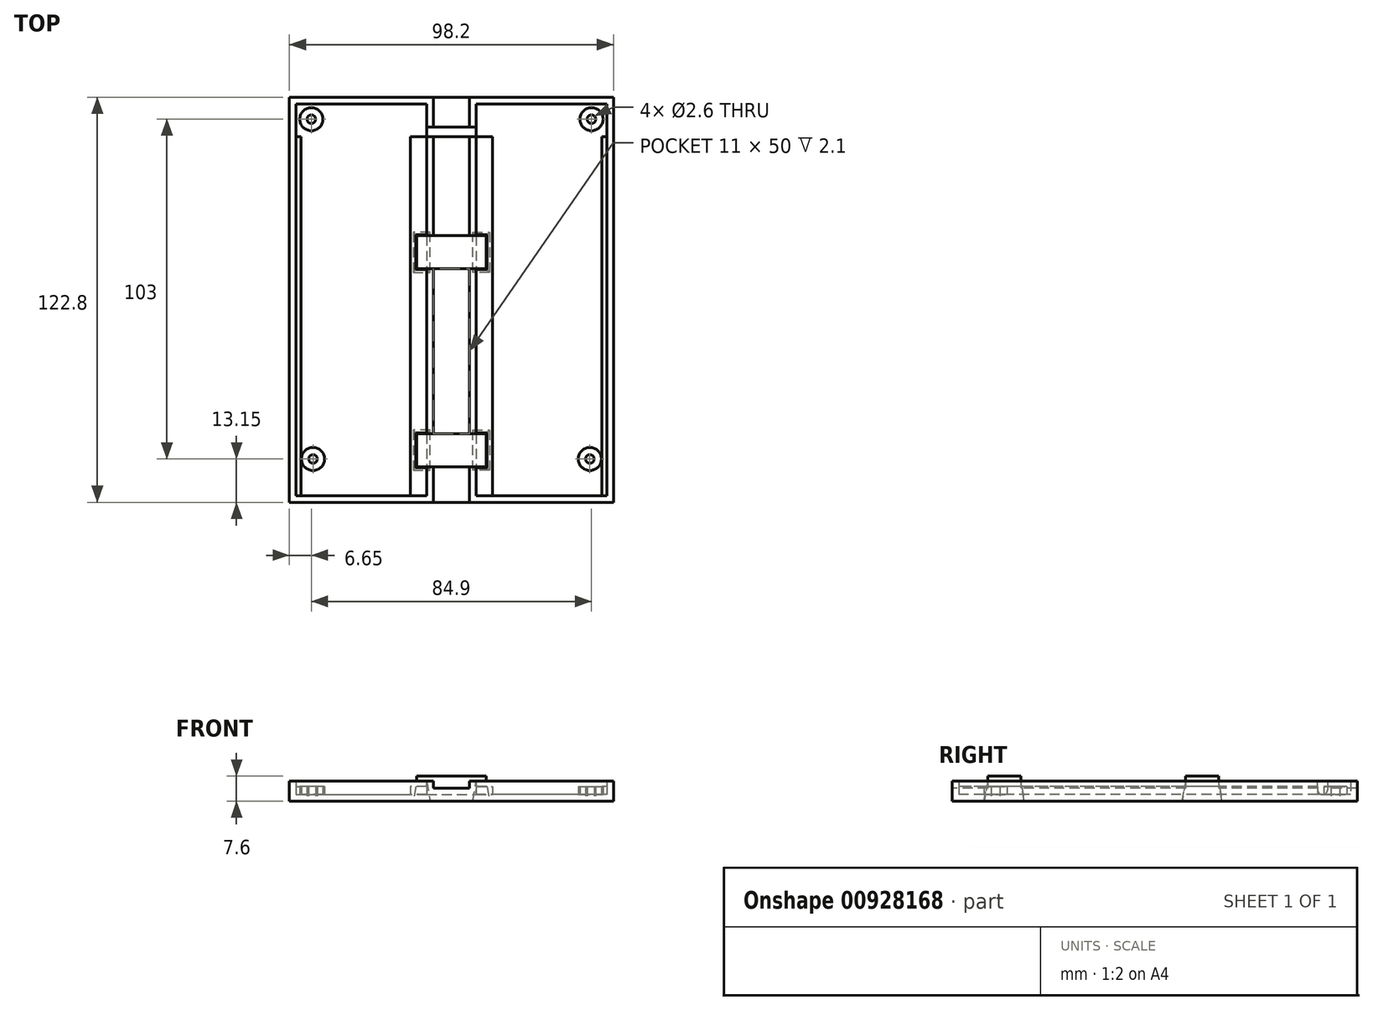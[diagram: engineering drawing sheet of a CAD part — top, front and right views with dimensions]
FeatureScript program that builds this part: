
annotation { "Feature Type Name" : "Feature", "Feature Type Description" : "" }
export const myFeature = defineFeature(function(context is Context, id is Id, definition is map)
    precondition{}
    {
        {
            var Q0;
            Q0=qCreatedBy(makeId("Top.planeOp"),FACE);
            var sketch = newSketch(context, id + "F0", { "sketchPlane" : qUnion([Q0])});
            skLineSegment(sketch, "E0.bottom", {"start": v(-49.1, 61.4) * mm, "end": v(-5.5, 61.4) * mm});
            skLineSegment(sketch, "E0.top", {"start": v(-49.1, -61.4) * mm, "end": v(-5.5, -61.4) * mm});
            skLineSegment(sketch, "E0.left", {"start": v(-49.1, 61.4) * mm, "end": v(-49.1, -61.4) * mm});
            skLineSegment(sketch, "E0.right", {"start": v(-5.5, 61.4) * mm, "end": v(-5.5, -61.4) * mm});
            skLineSegment(sketch, "E1", {"start": v(-5.5, 61.4) * mm, "end": v(0, 61.4) * mm});
            skLineSegment(sketch, "E2", {"start": v(0, 61.4) * mm, "end": v(0, -61.4) * mm});
            skLineSegment(sketch, "E3", {"start": v(0, -61.4) * mm, "end": v(-5.5, -61.4) * mm});
            skSolve(sketch);
        }
        {
            var Q0;
            Q0=makeQuery(id+"F0.imprint","IMPRINT",FACE,{"disambiguationData":[TD([[makeQuery(id+"F0.imprint","IMPRINT",EDGE,{"derivedFrom":sQuery(id+"F0.wireOp",EDGE,"E0.bottom")}),-1.0]])]});
            extrude(context, id + "F1", {"entities" : qUnion([Q0]), "depth" : 6.1 * mm, "offsetDistance" : 25 * mm});
        }
        {
            var Q0;
            Q0=makeQuery(id+"F1.opExtrude","CAP_FACE",FACE,{"disambiguationData":[OSD([sQuery(id+"F0.wireOp",EDGE,"E0.bottom"),sQuery(id+"F0.wireOp",EDGE,"E0.top"),sQuery(id+"F0.wireOp",EDGE,"E0.left"),sQuery(id+"F0.wireOp",EDGE,"E0.right")])],"isStart":false});
            shell(context, id + "F2", {"entities" : qUnion([Q0]), "thickness" : 2 * mm});
        }
        {
            var Q0;
            Q0=makeQuery(id+"F2.opShell","OFFSET_FACE",FACE,{"disambiguationData":[OSD([sQuery(id+"F0.wireOp",EDGE,"E0.bottom"),sQuery(id+"F0.wireOp",EDGE,"E0.top"),sQuery(id+"F0.wireOp",EDGE,"E0.left"),sQuery(id+"F0.wireOp",EDGE,"E0.right")])]});
            var sketch = newSketch(context, id + "F3", { "sketchPlane" : qUnion([Q0])});
            skCircle(sketch, "E4", {"center": v(-42.45, 54.75) * mm, "radius": 3.5 * mm});
            skCircle(sketch, "E5", {"center": v(-42.45, 54.75) * mm, "radius": 1.3 * mm});
            skLineSegment(sketch, "E6", {"start": v(-42.45, 54.75) * mm, "end": v(-47.1, 54.75) * mm, "construction": true});
            skLineSegment(sketch, "E7", {"start": v(-42.45, 54.75) * mm, "end": v(-42.45, 59.4) * mm, "construction": true});
            skCircle(sketch, "E8", {"center": v(-41.95, -48.25) * mm, "radius": 3.5 * mm});
            skCircle(sketch, "E9", {"center": v(-41.95, -48.25) * mm, "radius": 1.3 * mm});
            skLineSegment(sketch, "E10", {"start": v(-42.45, 54.75) * mm, "end": v(-42.45, -48.25) * mm, "construction": true});
            skLineSegment(sketch, "E11", {"start": v(-42.45, -48.25) * mm, "end": v(-41.95, -48.25) * mm, "construction": true});
            skSolve(sketch);
        }
        {
            var Q0;
            Q0 = qSketchRegion(id + "F3", true);
            var Q1;
            Q1=makeQuery(id+"F1.opExtrude","CAP_FACE",FACE,{"disambiguationData":[OSD([sQuery(id+"F0.wireOp",EDGE,"E0.bottom"),sQuery(id+"F0.wireOp",EDGE,"E0.top"),sQuery(id+"F0.wireOp",EDGE,"E0.left"),sQuery(id+"F0.wireOp",EDGE,"E0.right")])],"isStart":false});
            extrude(context, id + "F4", {"entities" : qUnion([Q0]), "operationType" : NewBodyOperationType.ADD, "endBound" : BoundingType.UP_TO_SURFACE, "depth" : 25 * mm, "endBoundEntityFace" : qUnion([Q1]), "hasOffset" : true, "offsetDistance" : 1.6 * mm});
        }
        {
            var Q0;
            Q0=makeQuery(id+"F4.boolean.opBoolean","SPLIT",FACE,{"disambiguationData":[TD([makeQuery(id+"F4.opExtrude","SWEPT_FACE",FACE,{"disambiguationData":[OSD([sQuery(id+"F3.wireOp",EDGE,"E5")])]})])],"derivedFrom":makeQuery(id+"F2.opShell","OFFSET_FACE",FACE,{"disambiguationData":[OSD([sQuery(id+"F0.wireOp",EDGE,"E0.bottom"),sQuery(id+"F0.wireOp",EDGE,"E0.top"),sQuery(id+"F0.wireOp",EDGE,"E0.left"),sQuery(id+"F0.wireOp",EDGE,"E0.right")])]})});
            var Q1;
            Q1=makeQuery(id+"F4.boolean.opBoolean","SPLIT",FACE,{"disambiguationData":[TD([makeQuery(id+"F4.opExtrude","SWEPT_FACE",FACE,{"disambiguationData":[OSD([sQuery(id+"F3.wireOp",EDGE,"E9")])]})])],"derivedFrom":makeQuery(id+"F2.opShell","OFFSET_FACE",FACE,{"disambiguationData":[OSD([sQuery(id+"F0.wireOp",EDGE,"E0.bottom"),sQuery(id+"F0.wireOp",EDGE,"E0.top"),sQuery(id+"F0.wireOp",EDGE,"E0.left"),sQuery(id+"F0.wireOp",EDGE,"E0.right")])]})});
            extrude(context, id + "F5", {"entities" : qUnion([Q0, Q1]), "operationType" : NewBodyOperationType.REMOVE, "endBound" : BoundingType.THROUGH_ALL, "oppositeDirection" : true, "depth" : 25 * mm, "offsetDistance" : 25 * mm});
        }
        {
            var Q0;
            {var subQ0=sQuery(id+"F0.wireOp",EDGE,"E0.right");var subQ1=sQuery(id+"F0.wireOp",EDGE,"E0.left");var subQ2=sQuery(id+"F0.wireOp",EDGE,"E0.top");var subQ3=sQuery(id+"F0.wireOp",EDGE,"E0.bottom");Q0=makeQuery(id+"F4.boolean.opBoolean","SPLIT",FACE,{"disambiguationData":[TD([makeQuery(id+"F2.opShell","OFFSET_FACE",FACE,{"disambiguationData":[OSD([subQ3])]})])],"derivedFrom":makeQuery(id+"F2.opShell","OFFSET_FACE",FACE,{"disambiguationData":[OSD([subQ3,subQ2,subQ1,subQ0])]})});}
            var sketch = newSketch(context, id + "F6", { "sketchPlane" : qUnion([Q0])});
            skLineSegment(sketch, "E12.bottom", {"start": v(-47.1, 49.4) * mm, "end": v(-45.6, 49.4) * mm});
            skLineSegment(sketch, "E12.top", {"start": v(-47.1, -59.4) * mm, "end": v(-45.6, -59.4) * mm});
            skLineSegment(sketch, "E12.left", {"start": v(-47.1, 49.4) * mm, "end": v(-47.1, -59.4) * mm});
            skLineSegment(sketch, "E12.right", {"start": v(-45.6, 49.4) * mm, "end": v(-45.6, -59.4) * mm});
            skLineSegment(sketch, "E13.bottom", {"start": v(-7.5, 49.4) * mm, "end": v(-12.5, 49.4) * mm});
            skLineSegment(sketch, "E13.top", {"start": v(-7.5, -59.4) * mm, "end": v(-12.5, -59.4) * mm});
            skLineSegment(sketch, "E13.left", {"start": v(-7.5, 49.4) * mm, "end": v(-7.5, -59.4) * mm});
            skLineSegment(sketch, "E13.right", {"start": v(-12.5, 49.4) * mm, "end": v(-12.5, -59.4) * mm});
            skLineSegment(sketch, "E14", {"start": v(-45.6, 49.4) * mm, "end": v(-12.5, 49.4) * mm, "construction": true});
            skSolve(sketch);
        }
        {
            var Q0;
            Q0 = qSketchRegion(id + "F6", true);
            var Q1;
            Q1=makeQuery(id+"F4.opExtrude","CAP_FACE",FACE,{"disambiguationData":[OSD([sQuery(id+"F3.wireOp",EDGE,"E4"),sQuery(id+"F3.wireOp",EDGE,"E5")])],"isStart":false});
            extrude(context, id + "F7", {"entities" : qUnion([Q0]), "operationType" : NewBodyOperationType.ADD, "endBound" : BoundingType.UP_TO_SURFACE, "depth" : 25 * mm, "endBoundEntityFace" : qUnion([Q1]), "offsetDistance" : 25 * mm});
        }
        {
            var Q0;
            Q0=makeQuery(id+"F1.opExtrude","CAP_FACE",FACE,{"disambiguationData":[OSD([sQuery(id+"F0.wireOp",EDGE,"E0.bottom"),sQuery(id+"F0.wireOp",EDGE,"E0.top"),sQuery(id+"F0.wireOp",EDGE,"E0.left"),sQuery(id+"F0.wireOp",EDGE,"E0.right")])],"isStart":false});
            var sketch = newSketch(context, id + "F8", { "sketchPlane" : qUnion([Q0])});
            skLineSegment(sketch, "E15.bottom", {"start": v(-10.5, 19.4) * mm, "end": v(-5.5, 19.4) * mm});
            skLineSegment(sketch, "E15.top", {"start": v(-10.5, 9.4) * mm, "end": v(-5.5, 9.4) * mm});
            skLineSegment(sketch, "E15.left", {"start": v(-10.5, 19.4) * mm, "end": v(-10.5, 9.4) * mm});
            skLineSegment(sketch, "E15.right", {"start": v(-5.5, 19.4) * mm, "end": v(-5.5, 9.4) * mm});
            skLineSegment(sketch, "E16.bottom", {"start": v(-10.5, -40.6) * mm, "end": v(-5.5, -40.6) * mm});
            skLineSegment(sketch, "E16.top", {"start": v(-10.5, -50.6) * mm, "end": v(-5.5, -50.6) * mm});
            skLineSegment(sketch, "E16.left", {"start": v(-10.5, -40.6) * mm, "end": v(-10.5, -50.6) * mm});
            skLineSegment(sketch, "E16.right", {"start": v(-5.5, -40.6) * mm, "end": v(-5.5, -50.6) * mm});
            skLineSegment(sketch, "E17", {"start": v(-10.5, -40.6) * mm, "end": v(-10.5, 9.4) * mm, "construction": true});
            skSolve(sketch);
        }
        {
            var Q0;
            Q0 = qSketchRegion(id + "F8", true);
            extrude(context, id + "F9", {"entities" : qUnion([Q0]), "operationType" : NewBodyOperationType.ADD, "depth" : 1.5 * mm, "offsetDistance" : 25 * mm});
        }
        {
            var Q0;
            Q0=makeQuery(id+"F9.opExtrude","CAP_FACE",FACE,{"disambiguationData":[OSD([sQuery(id+"F8.wireOp",EDGE,"E15.bottom"),sQuery(id+"F8.wireOp",EDGE,"E15.top"),sQuery(id+"F8.wireOp",EDGE,"E15.left"),sQuery(id+"F8.wireOp",EDGE,"E15.right")])],"isStart":true});
            var sketch = newSketch(context, id + "F10", { "sketchPlane" : qUnion([Q0])});
            skLineSegment(sketch, "E18.bottom", {"start": v(-10.5, -19.4) * mm, "end": v(-7.5, -19.4) * mm});
            skLineSegment(sketch, "E18.top", {"start": v(-10.5, -9.4) * mm, "end": v(-7.5, -9.4) * mm});
            skLineSegment(sketch, "E18.left", {"start": v(-10.5, -19.4) * mm, "end": v(-10.5, -9.4) * mm});
            skLineSegment(sketch, "E18.right", {"start": v(-7.5, -19.4) * mm, "end": v(-7.5, -9.4) * mm});
            skPoint(sketch, "E19.0", {"position": v(-10.5, 40.6) * mm});
            skPoint(sketch, "E19.1", {"position": v(-7.5, 50.6) * mm});
            skLineSegment(sketch, "E20.bottom", {"start": v(-10.5, 40.6) * mm, "end": v(-7.5, 40.6) * mm});
            skLineSegment(sketch, "E20.top", {"start": v(-10.5, 50.6) * mm, "end": v(-7.5, 50.6) * mm});
            skLineSegment(sketch, "E20.left", {"start": v(-10.5, 40.6) * mm, "end": v(-10.5, 50.6) * mm});
            skLineSegment(sketch, "E20.right", {"start": v(-7.5, 40.6) * mm, "end": v(-7.5, 50.6) * mm});
            skSolve(sketch);
        }
        {
            var Q0;
            Q0 = qSketchRegion(id + "F10", true);
            extrude(context, id + "F11", {"entities" : qUnion([Q0]), "operationType" : NewBodyOperationType.REMOVE, "depth" : 25 * mm, "offsetDistance" : 25 * mm, "hasDraft" : true, "draftAngle" : 10 * degree});
        }
        {
            var Q0;
            Q0=makeQuery(id+"F0.imprint","IMPRINT",FACE,{"disambiguationData":[TD([[makeQuery(id+"F0.imprint","IMPRINT",EDGE,{"derivedFrom":sQuery(id+"F0.wireOp",EDGE,"E0.right")}),1.0]])]});
            extrude(context, id + "F12", {"entities" : qUnion([Q0]), "operationType" : NewBodyOperationType.ADD, "depth" : 4 * mm, "offsetDistance" : 25 * mm});
        }
        {
            var Q0;
            Q0=makeQuery(id+"F12.opExtrude","SWEPT_FACE",FACE,{"disambiguationData":[OSD([sQuery(id+"F0.wireOp",EDGE,"E2")])]});
            var sketch = newSketch(context, id + "F13", { "sketchPlane" : qUnion([Q0])});
            skLineSegment(sketch, "E21.bottom", {"start": v(49.4, 4) * mm, "end": v(52.4, 4) * mm, "construction": true});
            skLineSegment(sketch, "E21.top", {"start": v(49.4, 3.5) * mm, "end": v(52.4, 3.5) * mm, "construction": true});
            skLineSegment(sketch, "E21.left", {"start": v(49.4, 4) * mm, "end": v(49.4, 3.5) * mm});
            skLineSegment(sketch, "E21.right", {"start": v(52.4, 4) * mm, "end": v(52.4, 3.5) * mm});
            skArc(sketch, "E22", {"start": v(49.4, 3.5) * mm, "mid": v(50.9, 2) * mm, "end": v(52.4, 3.5) * mm});
            skLineSegment(sketch, "E23", {"start": v(49.4, 4) * mm, "end": v(49.4, 7) * mm});
            skLineSegment(sketch, "E24", {"start": v(49.4, 7) * mm, "end": v(52.4, 7) * mm});
            skLineSegment(sketch, "E25", {"start": v(52.4, 7) * mm, "end": v(52.4, 4) * mm});
            skSolve(sketch);
        }
        {
            var Q0;
            Q0 = qSketchRegion(id + "F13", true);
            extrude(context, id + "F14", {"entities" : qUnion([Q0]), "operationType" : NewBodyOperationType.REMOVE, "oppositeDirection" : true, "depth" : 15 * mm, "offsetDistance" : 25 * mm});
        }
        {
            var Q0;
            Q0=makeQuery(id+"F1.opExtrude","SWEPT_BODY",BODY,{"disambiguationData":[OSD([sQuery(id+"F0.wireOp",EDGE,"E0.bottom"),sQuery(id+"F0.wireOp",EDGE,"E0.top"),sQuery(id+"F0.wireOp",EDGE,"E0.left"),sQuery(id+"F0.wireOp",EDGE,"E0.right")])]});
            var Q1;
            Q1=qCreatedBy(makeId("Right.planeOp"),FACE);
            mirror(context, id + "F15", {"operationType" : NewBodyOperationType.ADD, "entities" : qUnion([Q0]), "mirrorPlane" : qUnion([Q1])});
        }
        {
            var Q0;
            {var subQ2=sQuery(id+"F8.wireOp",EDGE,"E16.right");var subQ4=sQuery(id+"F0.wireOp",EDGE,"E0.right");var subQ6=sQuery(id+"F0.wireOp",EDGE,"E0.top");var subQ8=sQuery(id+"F8.wireOp",EDGE,"E15.right");Q0=makeQuery(id+"F14.boolean.opBoolean","SPLIT",FACE,{"disambiguationData":[TD([makeQuery(id+"F1.opExtrude","SWEPT_FACE",FACE,{"disambiguationData":[OSD([subQ6])]})])],"derivedFrom":makeQuery(id+"F9.boolean.opBoolean","MERGE",FACE,{"derivedFrom":[makeQuery(id+"F1.opExtrude","SWEPT_FACE",FACE,{"disambiguationData":[OSD([subQ4])]}),makeQuery(id+"F9.opExtrude","SWEPT_FACE",FACE,{"disambiguationData":[OSD([subQ8])]}),makeQuery(id+"F9.opExtrude","SWEPT_FACE",FACE,{"disambiguationData":[OSD([subQ2])]})]})});}
            var sketch = newSketch(context, id + "F16", { "sketchPlane" : qUnion([Q0])});
            skLineSegment(sketch, "E26.bottom", {"start": v(19.4, 7.6) * mm, "end": v(9.4, 7.6) * mm});
            skLineSegment(sketch, "E26.top", {"start": v(19.4, 4) * mm, "end": v(9.4, 4) * mm});
            skLineSegment(sketch, "E26.left", {"start": v(19.4, 7.6) * mm, "end": v(19.4, 4) * mm});
            skLineSegment(sketch, "E26.right", {"start": v(9.4, 7.6) * mm, "end": v(9.4, 4) * mm});
            skLineSegment(sketch, "E27.bottom", {"start": v(-40.6, 7.6) * mm, "end": v(-50.6, 7.6) * mm});
            skLineSegment(sketch, "E27.top", {"start": v(-40.6, 4) * mm, "end": v(-50.6, 4) * mm});
            skLineSegment(sketch, "E27.left", {"start": v(-40.6, 7.6) * mm, "end": v(-40.6, 4) * mm});
            skLineSegment(sketch, "E27.right", {"start": v(-50.6, 7.6) * mm, "end": v(-50.6, 4) * mm});
            skSolve(sketch);
        }
        {
            var Q0;
            Q0 = qSketchRegion(id + "F16", true);
            extrude(context, id + "F17", {"entities" : qUnion([Q0]), "operationType" : NewBodyOperationType.ADD, "endBound" : BoundingType.UP_TO_NEXT, "depth" : 25 * mm, "offsetDistance" : 25 * mm});
        }
    });
